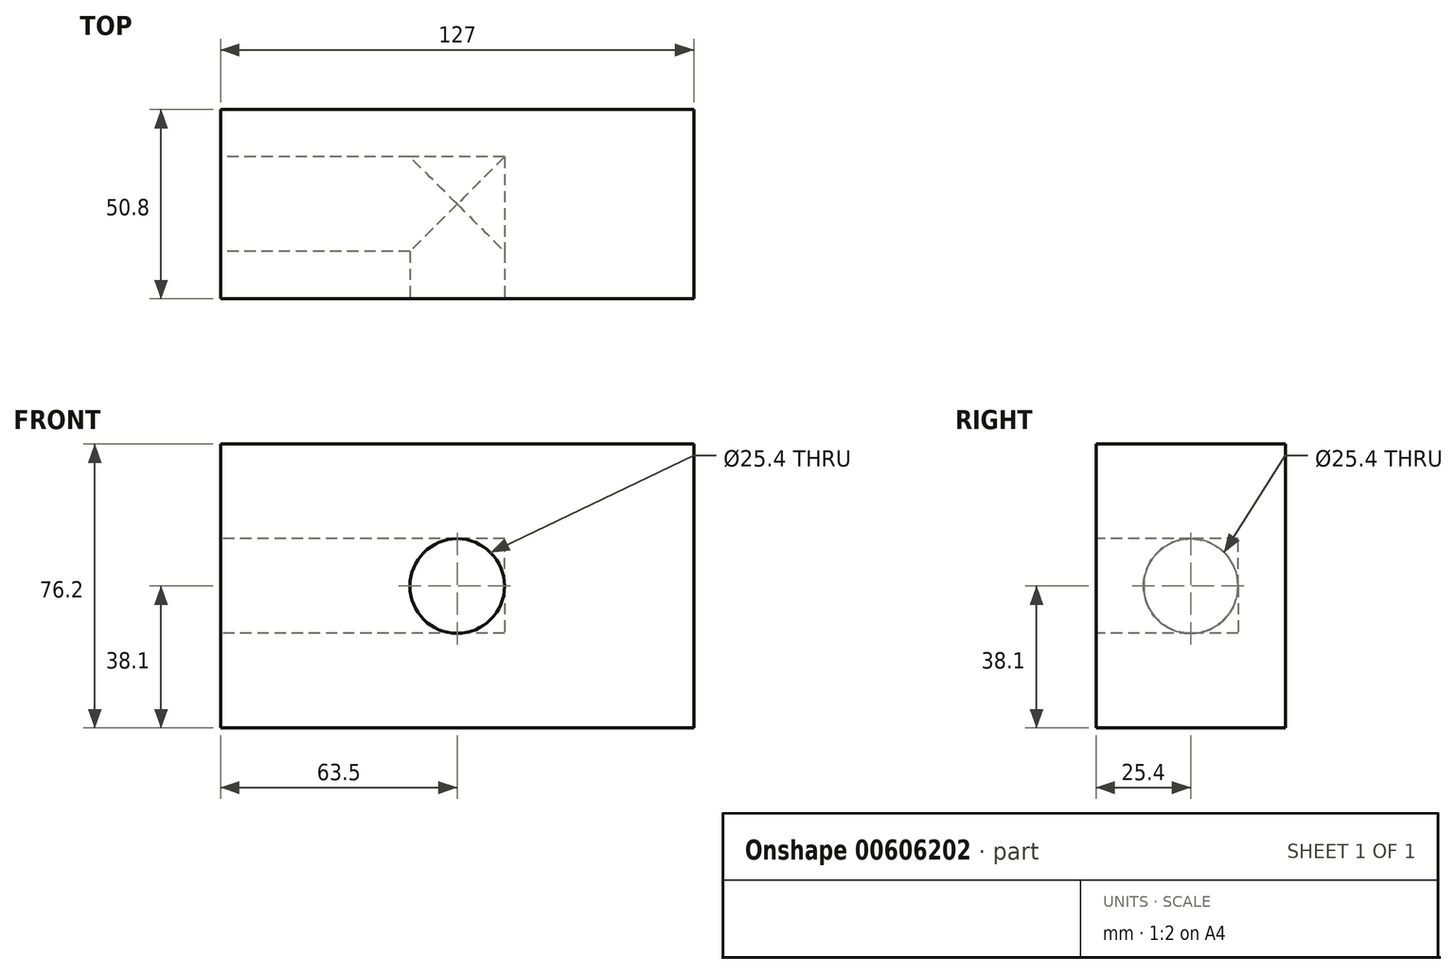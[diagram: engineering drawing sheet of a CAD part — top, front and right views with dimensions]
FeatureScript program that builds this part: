
annotation { "Feature Type Name" : "Feature", "Feature Type Description" : "" }
export const myFeature = defineFeature(function(context is Context, id is Id, definition is map)
    precondition{}
    {
        {
            var Q0;
            Q0=qCreatedBy(makeId("Front.planeOp"),FACE);
            var sketch = newSketch(context, id + "F0", { "sketchPlane" : qUnion([Q0])});
            skLineSegment(sketch, "E0.bottom", {"start": v(-63.5, 38.1) * mm, "end": v(63.5, 38.1) * mm});
            skLineSegment(sketch, "E0.top", {"start": v(-63.5, -38.1) * mm, "end": v(63.5, -38.1) * mm});
            skLineSegment(sketch, "E0.left", {"start": v(-63.5, 38.1) * mm, "end": v(-63.5, -38.1) * mm});
            skLineSegment(sketch, "E0.right", {"start": v(63.5, 38.1) * mm, "end": v(63.5, -38.1) * mm});
            skPoint(sketch, "E0.middle", {"position": v(0, 0) * mm});
            skSolve(sketch);
        }
        {
            var Q0;
            Q0 = qSketchRegion(id + "F0", true);
            extrude(context, id + "F1", {"entities" : qUnion([Q0]), "depth" : 50.8 * mm, "offsetDistance" : 25.4 * mm});
        }
        {
            var Q0;
            Q0=makeQuery(id+"F1.opExtrude","CAP_FACE",FACE,{"disambiguationData":[OSD([sQuery(id+"F0.wireOp",EDGE,"E0.bottom"),sQuery(id+"F0.wireOp",EDGE,"E0.top"),sQuery(id+"F0.wireOp",EDGE,"E0.left"),sQuery(id+"F0.wireOp",EDGE,"E0.right")])],"isStart":false});
            var sketch = newSketch(context, id + "F2", { "sketchPlane" : qUnion([Q0])});
            skCircle(sketch, "E1", {"center": v(0, 0) * mm, "radius": 12.7 * mm});
            skSolve(sketch);
        }
        {
            var Q0;
            Q0 = qSketchRegion(id + "F2", true);
            extrude(context, id + "F3", {"entities" : qUnion([Q0]), "operationType" : NewBodyOperationType.REMOVE, "oppositeDirection" : true, "depth" : 38.1 * mm, "offsetDistance" : 25.4 * mm});
        }
        {
            var Q0;
            Q0=makeQuery(id+"F1.opExtrude","SWEPT_FACE",FACE,{"disambiguationData":[OSD([sQuery(id+"F0.wireOp",EDGE,"E0.left")])]});
            var sketch = newSketch(context, id + "F4", { "sketchPlane" : qUnion([Q0])});
            skCircle(sketch, "E2", {"center": v(25.4, 0) * mm, "radius": 12.7 * mm});
            skSolve(sketch);
        }
        {
            var Q0;
            Q0 = qSketchRegion(id + "F4", true);
            extrude(context, id + "F5", {"entities" : qUnion([Q0]), "operationType" : NewBodyOperationType.REMOVE, "oppositeDirection" : true, "depth" : 76.2 * mm, "offsetDistance" : 25.4 * mm});
        }
    });
